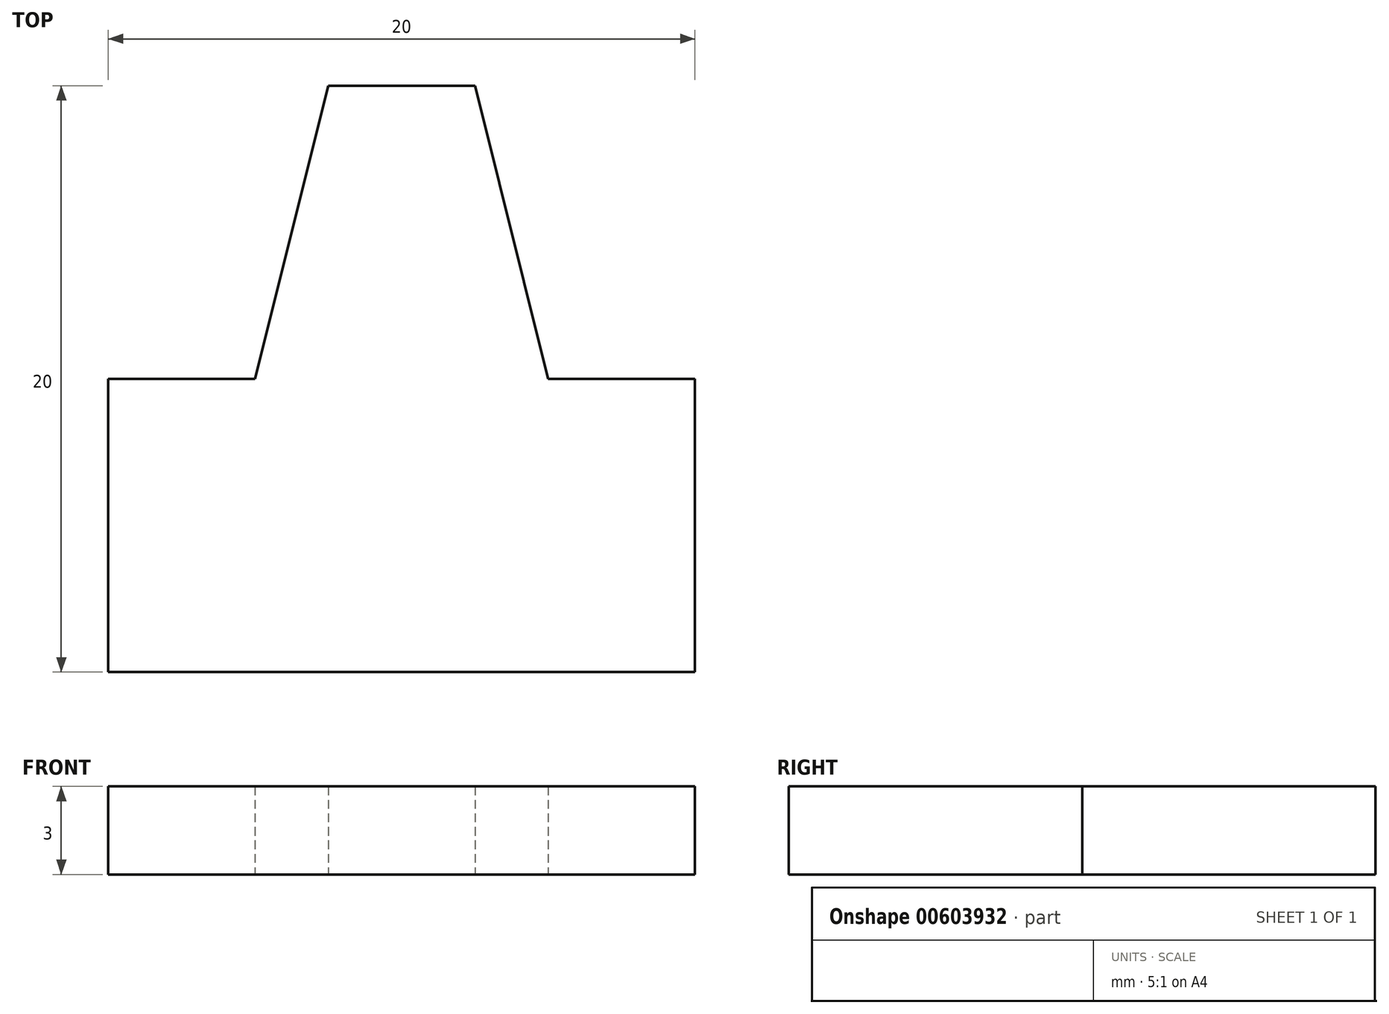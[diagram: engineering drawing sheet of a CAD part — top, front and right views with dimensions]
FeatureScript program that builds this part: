
annotation { "Feature Type Name" : "Feature", "Feature Type Description" : "" }
export const myFeature = defineFeature(function(context is Context, id is Id, definition is map)
    precondition{}
    {
        {
            var Q0;
            Q0=qCreatedBy(makeId("Top.planeOp"),FACE);
            var sketch = newSketch(context, id + "F0", { "sketchPlane" : qUnion([Q0])});
            skLineSegment(sketch, "E0", {"start": v(5, 0) * mm, "end": v(7.5, -10) * mm});
            skLineSegment(sketch, "E1", {"start": v(-2.5, -10) * mm, "end": v(0, 0) * mm});
            skLineSegment(sketch, "E2", {"start": v(0, 0) * mm, "end": v(5, 0) * mm});
            skLineSegment(sketch, "E3.bottom", {"start": v(-7.5, -10) * mm, "end": v(-2.5, -10) * mm});
            skLineSegment(sketch, "E3.top", {"start": v(-7.5, -20) * mm, "end": v(12.5, -20) * mm});
            skLineSegment(sketch, "E3.left", {"start": v(-7.5, -10) * mm, "end": v(-7.5, -20) * mm});
            skLineSegment(sketch, "E3.right", {"start": v(12.5, -10) * mm, "end": v(12.5, -20) * mm});
            skLineSegment(sketch, "E4.trimOffspring", {"start": v(7.5, -10) * mm, "end": v(12.5, -10) * mm});
            skSolve(sketch);
        }
        {
            var Q0;
            Q0 = qSketchRegion(id + "F0", true);
            extrude(context, id + "F1", {"entities" : qUnion([Q0]), "depth" : 3 * mm, "offsetDistance" : 25 * mm});
        }
    });
